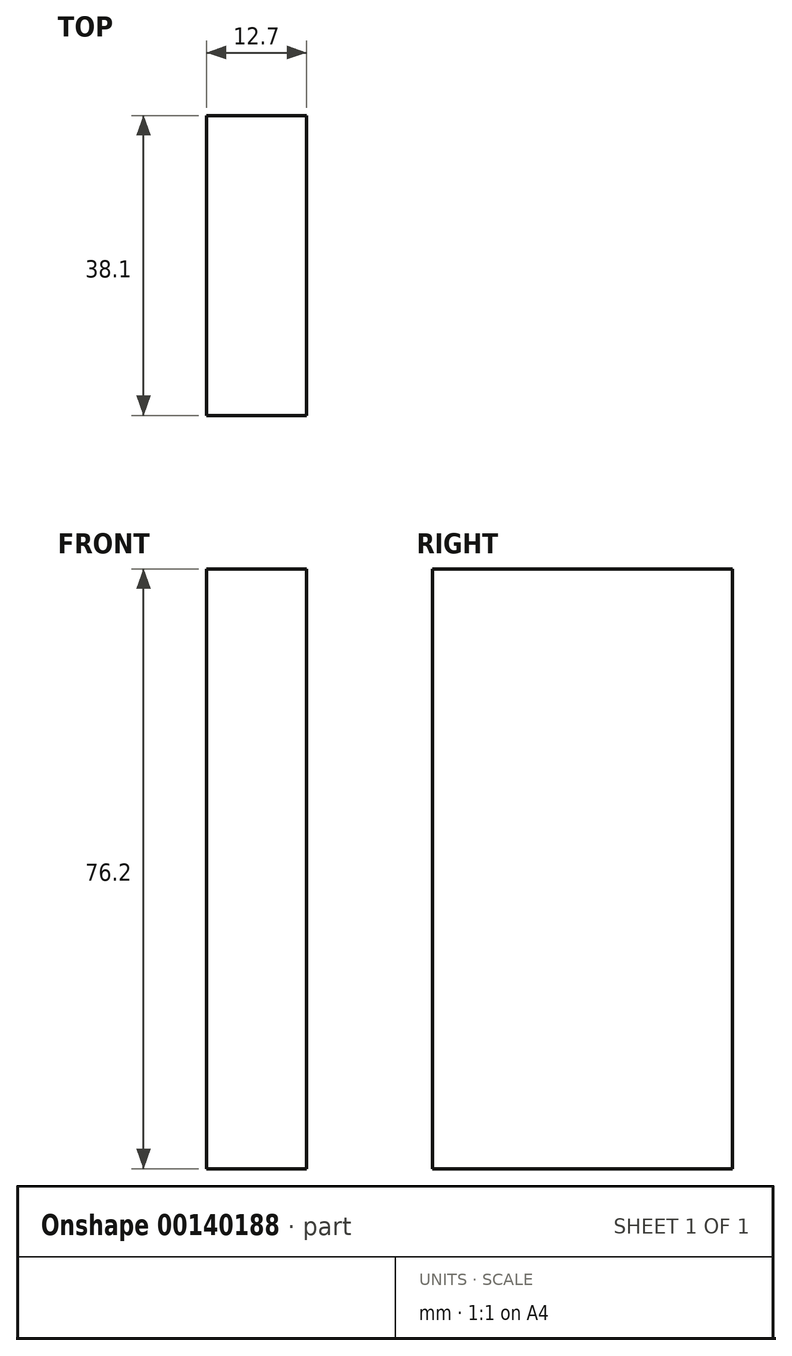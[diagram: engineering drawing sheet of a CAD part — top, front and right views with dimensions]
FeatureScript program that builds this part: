
annotation { "Feature Type Name" : "Feature", "Feature Type Description" : "" }
export const myFeature = defineFeature(function(context is Context, id is Id, definition is map)
    precondition{}
    {
        {
            var Q0;
            Q0=qCreatedBy(makeId("Right.planeOp"),FACE);
            var sketch = newSketch(context, id + "F0", { "sketchPlane" : qUnion([Q0])});
            skLineSegment(sketch, "E0.bottom", {"start": v(-18.75, 66.7) * mm, "end": v(19.35, 66.7) * mm});
            skLineSegment(sketch, "E0.top", {"start": v(-18.75, -9.5) * mm, "end": v(19.35, -9.5) * mm});
            skLineSegment(sketch, "E0.left", {"start": v(-18.75, 66.7) * mm, "end": v(-18.75, -9.5) * mm});
            skLineSegment(sketch, "E0.right", {"start": v(19.35, 66.7) * mm, "end": v(19.35, -9.5) * mm});
            skLineSegment(sketch, "E1.bottom", {"start": v(19.35, 66.7) * mm, "end": v(-18.75, 66.7) * mm});
            skLineSegment(sketch, "E1.top", {"start": v(19.35, 28.6) * mm, "end": v(-18.75, 28.6) * mm});
            skLineSegment(sketch, "E1.left", {"start": v(19.35, 66.7) * mm, "end": v(19.35, 28.6) * mm});
            skLineSegment(sketch, "E1.right", {"start": v(-18.75, 66.7) * mm, "end": v(-18.75, 28.6) * mm});
            skSolve(sketch);
        }
        {
            var Q0;
            Q0=qSketchRegion(id+"F0",true);
            extrude(context, id + "F1", {"entities" : qUnion([Q0]), "depth" : 12.7 * mm});
        }
        {
            var Q0;
            Q0=makeQuery(id+"F1.opExtrude","CAP_FACE",FACE,{"disambiguationData":[OSD([sQuery(id+"F0.wireOp",EDGE,"E0.top"),sQuery(id+"F0.wireOp",EDGE,"E0.left"),sQuery(id+"F0.wireOp",EDGE,"E0.right"),sQuery(id+"F0.wireOp",EDGE,"E1.bottom"),sQuery(id+"F0.wireOp",EDGE,"E1.left"),sQuery(id+"F0.wireOp",EDGE,"E1.right")])],"isStart":false});
            var sketch = newSketch(context, id + "F2", { "sketchPlane" : qUnion([Q0])});
            skLineSegment(sketch, "E2.bottom", {"start": v(-18.75, 66.7) * mm, "end": v(19.35, 66.7) * mm});
            skLineSegment(sketch, "E2.top", {"start": v(-18.75, 28.6) * mm, "end": v(19.35, 28.6) * mm});
            skLineSegment(sketch, "E2.left", {"start": v(-18.75, 66.7) * mm, "end": v(-18.75, 28.6) * mm});
            skLineSegment(sketch, "E2.right", {"start": v(19.35, 66.7) * mm, "end": v(19.35, 28.6) * mm});
            skSolve(sketch);
        }
    });
